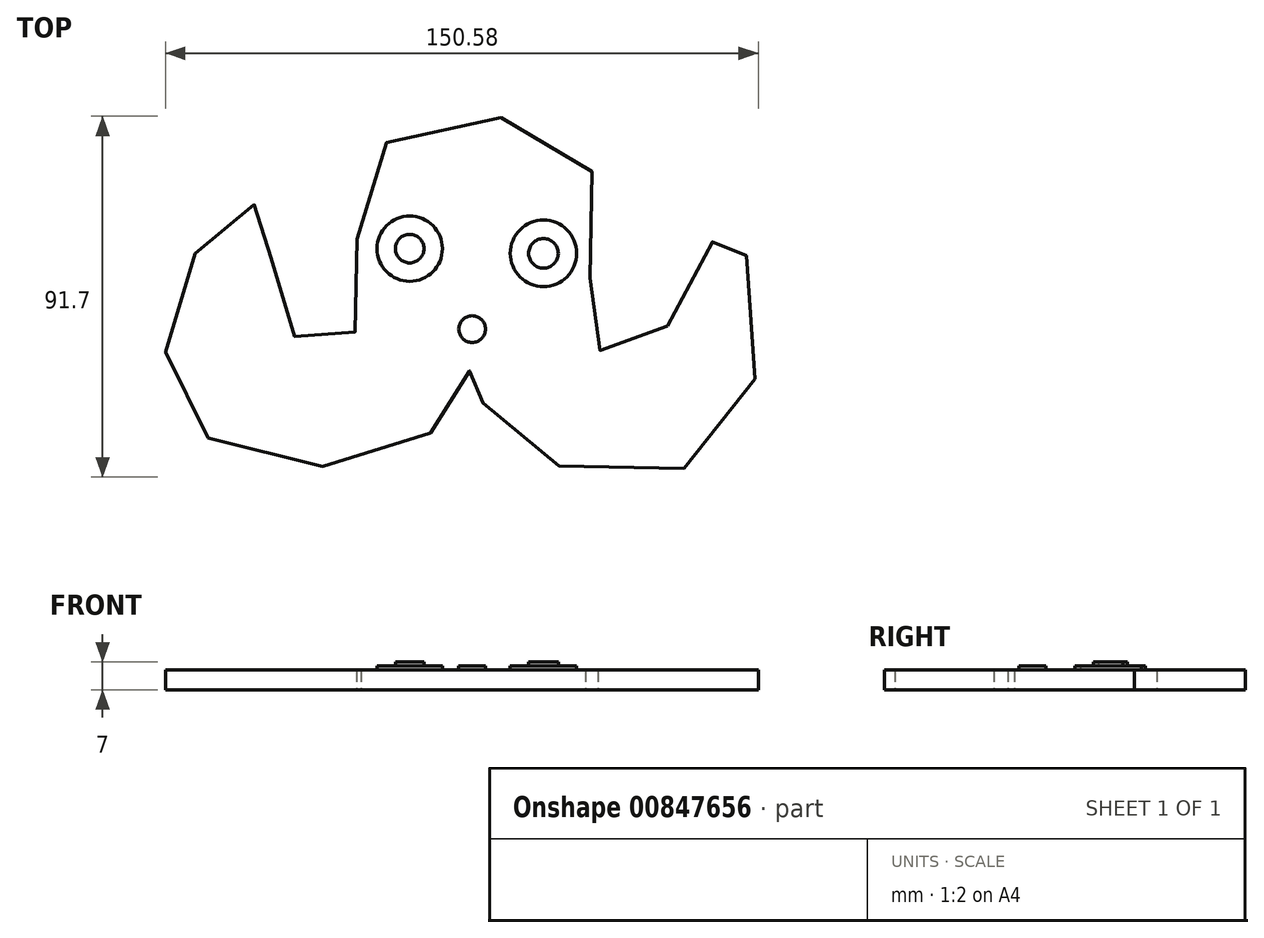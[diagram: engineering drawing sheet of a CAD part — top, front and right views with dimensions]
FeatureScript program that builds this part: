
annotation { "Feature Type Name" : "Feature", "Feature Type Description" : "" }
export const myFeature = defineFeature(function(context is Context, id is Id, definition is map)
    precondition{}
    {
        {
            var Q0;
            Q0=qCreatedBy(makeId("Top.planeOp"),FACE);
            var sketch = newSketch(context, id + "F0", { "sketchPlane" : qUnion([Q0])});
            skFitSpline(sketch, "E0", {"points": [v(-70.35, -6.57) * mm, v(-70.35, -50.78) * mm, v(-11.16, -52.68) * mm, v(0, -35.57) * mm, v(7.61, -52.2) * mm, v(66.32, -52.44) * mm, v(65.13, 0) * mm, v(48.5, -26.3) * mm, v(29.72, -28.44) * mm, v(28.77, 17.43) * mm, v(-24.95, 18.38) * mm, v(-30.18, -27.25) * mm, v(-48, -24.64) * mm, v(-52.76, 4.84) * mm, v(-70.35, -6.57) * mm]});
            skSolve(sketch);
        }
        {
            var Q0;
            Q0=makeQuery(id+"F0.imprint","IMPRINT",FACE,{"disambiguationData":[TD([[makeQuery(id+"F0.imprint","IMPRINT",EDGE,{"derivedFrom":sQuery(id+"F0.wireOp",EDGE,"E0")}),1.0]])]});
            extrude(context, id + "F1", {"entities" : qUnion([Q0]), "depth" : 5 * mm, "offsetDistance" : 25.4 * mm});
        }
        {
            var Q0;
            Q0=makeQuery(id+"F1.opExtrude","CAP_FACE",FACE,{"disambiguationData":[OSD([sQuery(id+"F0.wireOp",EDGE,"E0")])],"isStart":false});
            var sketch = newSketch(context, id + "F2", { "sketchPlane" : qUnion([Q0])});
            skCircle(sketch, "E1", {"center": v(18.13, -6.57) * mm, "radius": 8.44 * mm});
            skSolve(sketch);
        }
        {
            var Q0;
            Q0 = qSketchRegion(id + "F2", true);
            extrude(context, id + "F3", {"entities" : qUnion([Q0]), "operationType" : NewBodyOperationType.ADD, "depth" : 1 * mm, "offsetDistance" : 25 * mm});
        }
        {
            var Q0;
            Q0=makeQuery(id+"F1.opExtrude","CAP_FACE",FACE,{"disambiguationData":[OSD([sQuery(id+"F0.wireOp",EDGE,"E0")])],"isStart":false});
            var sketch = newSketch(context, id + "F4", { "sketchPlane" : qUnion([Q0])});
            skCircle(sketch, "E2", {"center": v(-15.86, -5.38) * mm, "radius": 8.3 * mm});
            skSolve(sketch);
        }
        {
            var Q0;
            Q0 = qSketchRegion(id + "F4", true);
            extrude(context, id + "F5", {"entities" : qUnion([Q0]), "operationType" : NewBodyOperationType.ADD, "depth" : 1 * mm, "offsetDistance" : 25 * mm});
        }
        {
            var Q0;
            Q0=makeQuery(id+"F1.opExtrude","CAP_FACE",FACE,{"disambiguationData":[OSD([sQuery(id+"F0.wireOp",EDGE,"E0")])],"isStart":false});
            var sketch = newSketch(context, id + "F6", { "sketchPlane" : qUnion([Q0])});
            skCircle(sketch, "E3", {"center": v(-15.86, -5.38) * mm, "radius": 3.63 * mm});
            skSolve(sketch);
        }
        {
            var Q0;
            Q0 = qSketchRegion(id + "F6", true);
            extrude(context, id + "F7", {"entities" : qUnion([Q0]), "operationType" : NewBodyOperationType.ADD, "depth" : 2 * mm, "offsetDistance" : 25 * mm});
        }
        {
            var Q0;
            Q0=makeQuery(id+"F1.opExtrude","CAP_FACE",FACE,{"disambiguationData":[OSD([sQuery(id+"F0.wireOp",EDGE,"E0")])],"isStart":false});
            var sketch = newSketch(context, id + "F8", { "sketchPlane" : qUnion([Q0])});
            skCircle(sketch, "E4", {"center": v(18.13, -6.57) * mm, "radius": 3.76 * mm});
            skSolve(sketch);
        }
        {
            var Q0;
            Q0 = qSketchRegion(id + "F8", true);
            extrude(context, id + "F9", {"entities" : qUnion([Q0]), "operationType" : NewBodyOperationType.ADD, "depth" : 2 * mm, "offsetDistance" : 25 * mm});
        }
        {
            var Q0;
            Q0=makeQuery(id+"F1.opExtrude","CAP_FACE",FACE,{"disambiguationData":[OSD([sQuery(id+"F0.wireOp",EDGE,"E0")])],"isStart":false});
            var sketch = newSketch(context, id + "F10", { "sketchPlane" : qUnion([Q0])});
            skCircle(sketch, "E5", {"center": v(0, -25.82) * mm, "radius": 3.39 * mm});
            skSolve(sketch);
        }
        {
            var Q0;
            Q0 = qSketchRegion(id + "F10", true);
            extrude(context, id + "F11", {"entities" : qUnion([Q0]), "operationType" : NewBodyOperationType.ADD, "depth" : 1 * mm, "offsetDistance" : 25 * mm});
        }
    });
